# Revit family: Lighting-WallMount-Amerlux-Linea 2.5
name_source: partatom
category: Lighting Fixtures
units: mm (PartAtom-declared; Revit-internal decimal feet)

## family parameters
Cut with Voids When Loaded = No
Host = Face
Light Source = Yes
Part Type = Normal
Room Calculation Point = No
Round Connector Dimension = Use Diameter
Shared = No

## types (1)
- Linea 2.5" Wall Mount
    Apparent Load = 0 VA
    Color Filter = 16777215
    Default Elevation = 4' - 0"
    Description = Linear Direct LED
    Dimming Lamp Color Temperature Shift = <None>
    Emit from Line Length = 4' - 0"
    Fixture Finish = Aluminum Finish
    Height = 0' - 3 1/2"
    Length = 4' - 0"
    Manufacturer = Amerlux
    Model = Linea 2.5" Wall Mount
    Number of Poles = 1
    Photometric Web File = Load File
    Power Factor = 1
    Tilt Angle = -90.00°
    URL = http://www.amerlux.com
    Voltage = 0 V
    Width = 0' - 2 11/16"

## geometry (parser evidence)
native form markers: Sweep x3
no freeform markers — native parametric forms only
